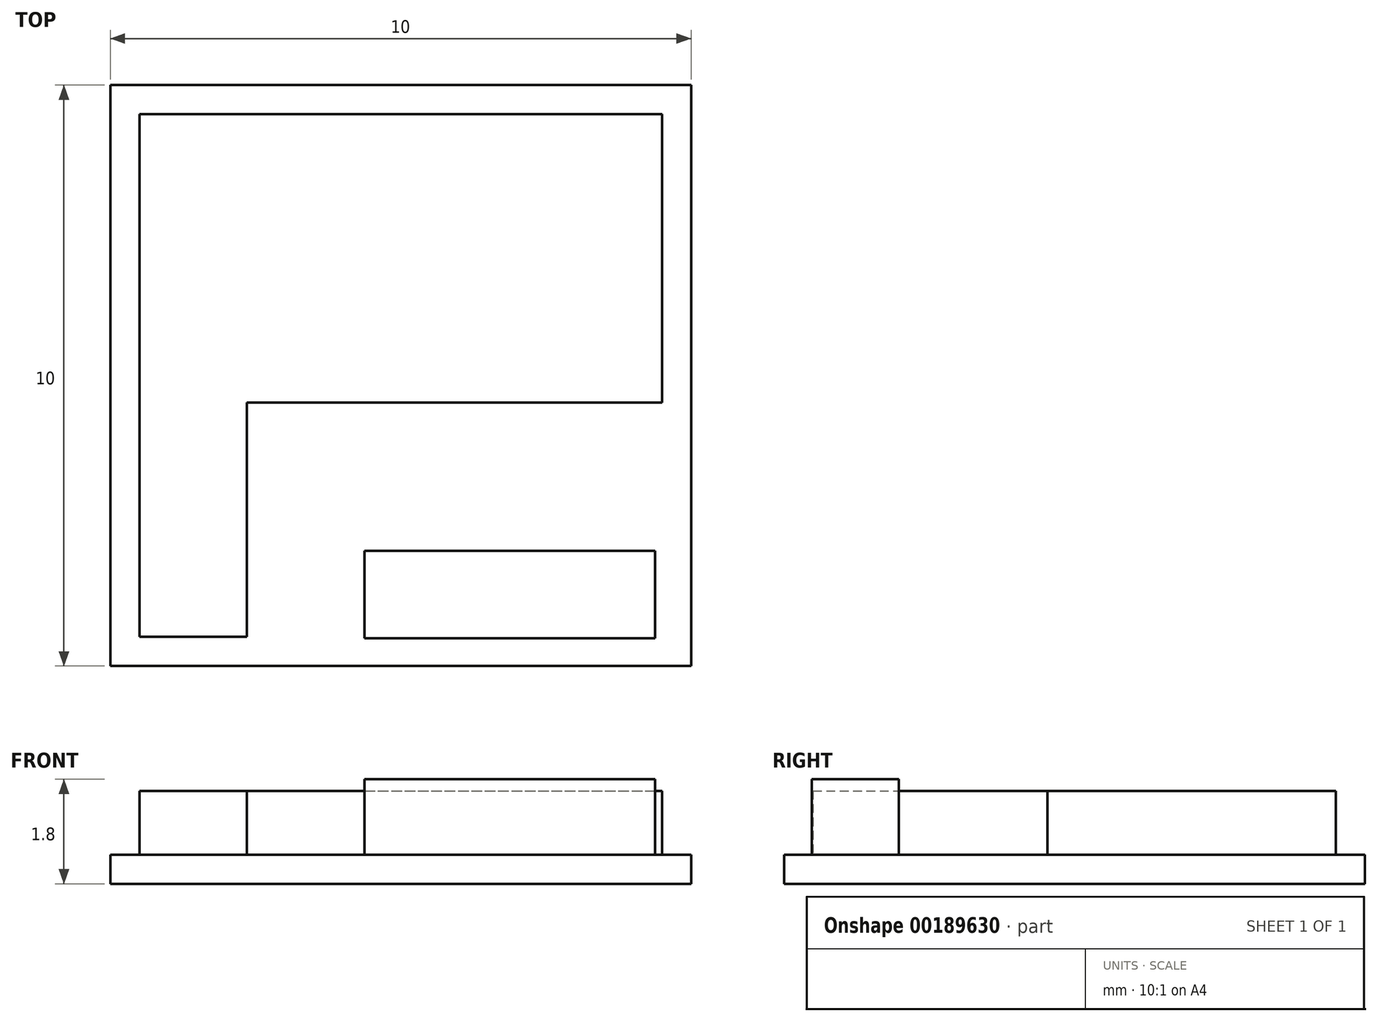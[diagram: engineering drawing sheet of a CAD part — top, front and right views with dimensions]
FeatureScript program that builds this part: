
annotation { "Feature Type Name" : "Feature", "Feature Type Description" : "" }
export const myFeature = defineFeature(function(context is Context, id is Id, definition is map)
    precondition{}
    {
        {
            var Q0;
            Q0=qCreatedBy(makeId("Top.planeOp"),FACE);
            var sketch = newSketch(context, id + "F0", { "sketchPlane" : qUnion([Q0])});
            skLineSegment(sketch, "E0.bottom", {"start": v(0, 0) * mm, "end": v(10, 0) * mm});
            skLineSegment(sketch, "E0.top", {"start": v(0, 10) * mm, "end": v(10, 10) * mm});
            skLineSegment(sketch, "E0.left", {"start": v(0, 0) * mm, "end": v(0, 10) * mm});
            skLineSegment(sketch, "E0.right", {"start": v(10, 0) * mm, "end": v(10, 10) * mm});
            skSolve(sketch);
        }
        {
            var Q0;
            Q0=qSketchRegion(id+"F0",true);
            extrude(context, id + "F1", {"entities" : qUnion([Q0]), "depth" : 0.5 * mm});
        }
        {
            var Q0;
            Q0=makeQuery(id+"F1.opExtrude","CAP_FACE",FACE,{"disambiguationData":[OSD([sQuery(id+"F0.wireOp",EDGE,"E0.bottom"),sQuery(id+"F0.wireOp",EDGE,"E0.top"),sQuery(id+"F0.wireOp",EDGE,"E0.left"),sQuery(id+"F0.wireOp",EDGE,"E0.right")])],"isStart":false});
            var sketch = newSketch(context, id + "F2", { "sketchPlane" : qUnion([Q0])});
            skLineSegment(sketch, "E1.0", {"start": v(0.5, 0.5) * mm, "end": v(0.5, 9.5) * mm});
            skLineSegment(sketch, "E1.1", {"start": v(0.5, 0.5) * mm, "end": v(2.35, 0.5) * mm});
            skLineSegment(sketch, "E1.2", {"start": v(9.5, 4.53) * mm, "end": v(9.5, 9.5) * mm});
            skLineSegment(sketch, "E1.3", {"start": v(0.5, 9.5) * mm, "end": v(9.5, 9.5) * mm});
            skLineSegment(sketch, "E2", {"start": v(2.35, 0.5) * mm, "end": v(2.35, 4.53) * mm});
            skLineSegment(sketch, "E3", {"start": v(2.35, 4.53) * mm, "end": v(9.5, 4.53) * mm});
            skSolve(sketch);
        }
        {
            var Q0;
            Q0=qSketchRegion(id+"F2",true);
            extrude(context, id + "F3", {"entities" : qUnion([Q0]), "operationType" : NewBodyOperationType.ADD, "depth" : 1.1 * mm});
        }
        {
            var Q0;
            Q0=makeQuery(id+"F1.opExtrude","CAP_FACE",FACE,{"disambiguationData":[OSD([sQuery(id+"F0.wireOp",EDGE,"E0.bottom"),sQuery(id+"F0.wireOp",EDGE,"E0.top"),sQuery(id+"F0.wireOp",EDGE,"E0.left"),sQuery(id+"F0.wireOp",EDGE,"E0.right")])],"isStart":false});
            var sketch = newSketch(context, id + "F4", { "sketchPlane" : qUnion([Q0])});
            skLineSegment(sketch, "E4.bottom", {"start": v(9.38, 0.48) * mm, "end": v(4.38, 0.48) * mm});
            skLineSegment(sketch, "E4.top", {"start": v(9.38, 1.98) * mm, "end": v(4.38, 1.98) * mm});
            skLineSegment(sketch, "E4.left", {"start": v(9.38, 0.48) * mm, "end": v(9.38, 1.98) * mm});
            skLineSegment(sketch, "E4.right", {"start": v(4.38, 0.48) * mm, "end": v(4.38, 1.98) * mm});
            skSolve(sketch);
        }
        {
            var Q0;
            Q0=qSketchRegion(id+"F4",true);
            extrude(context, id + "F5", {"entities" : qUnion([Q0]), "operationType" : NewBodyOperationType.ADD, "depth" : 1.3 * mm});
        }
    });
